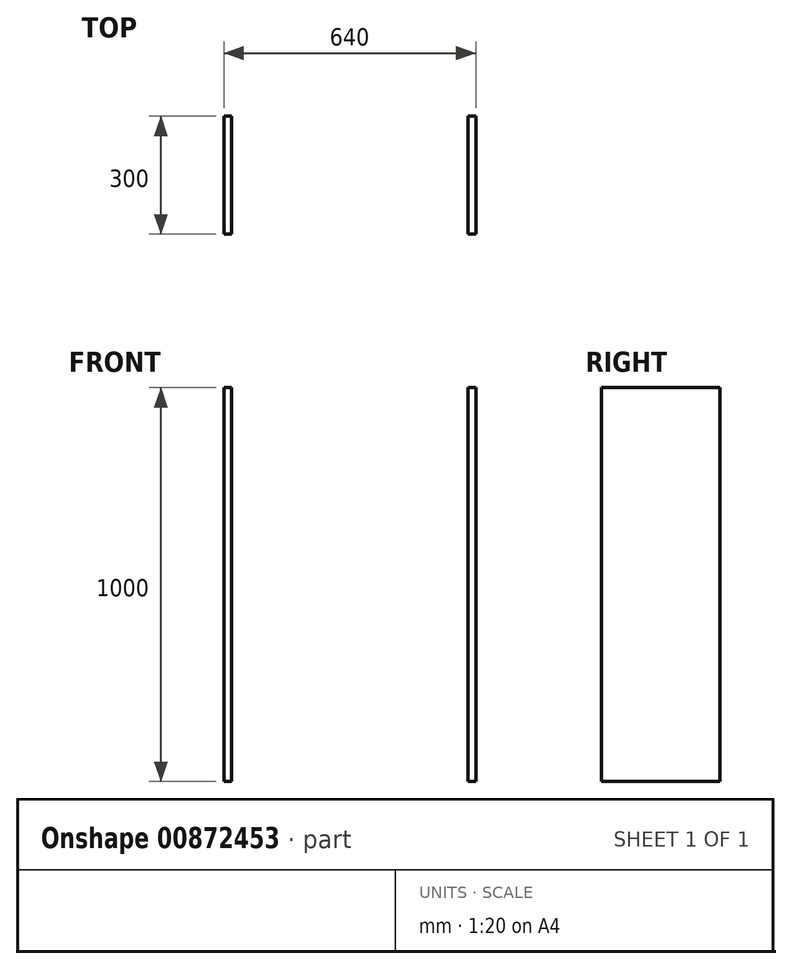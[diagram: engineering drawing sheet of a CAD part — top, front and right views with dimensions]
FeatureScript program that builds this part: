
annotation { "Feature Type Name" : "Feature", "Feature Type Description" : "" }
export const myFeature = defineFeature(function(context is Context, id is Id, definition is map)
    precondition{}
    {
        {
            var Q0;
            Q0=qCreatedBy(makeId("Right.planeOp"),FACE);
            cPlane(context, id + "F0", {"entities" : qUnion([Q0]), "cplaneType" : CPlaneType.OFFSET, "offset" : 300 * mm, "oppositeDirection" : true, "width" : 150 * mm, "height" : 150 * mm});
        }
        {
            var Q0;
            Q0=qCreatedBy(makeId("Right.planeOp"),FACE);
            cPlane(context, id + "F1", {"entities" : qUnion([Q0]), "cplaneType" : CPlaneType.OFFSET, "offset" : 300 * mm, "width" : 150 * mm, "height" : 150 * mm});
        }
        {
            var Q0;
            Q0=qCreatedBy(id+"F0.planeOp",FACE);
            var sketch = newSketch(context, id + "F2", { "sketchPlane" : qUnion([Q0])});
            skLineSegment(sketch, "E0", {"start": v(-400, 500) * mm, "end": v(-100, 500) * mm});
            skLineSegment(sketch, "E1", {"start": v(-100, 500) * mm, "end": v(-100, -500) * mm});
            skLineSegment(sketch, "E2", {"start": v(-100, -500) * mm, "end": v(-400, -500) * mm});
            skLineSegment(sketch, "E3", {"start": v(-400, -500) * mm, "end": v(-400, 500) * mm});
            skSolve(sketch);
        }
        {
            var Q0;
            Q0=qCreatedBy(id+"F1.planeOp",FACE);
            var sketch = newSketch(context, id + "F3", { "sketchPlane" : qUnion([Q0])});
            skLineSegment(sketch, "E4", {"start": v(-400, 500) * mm, "end": v(-100, 500) * mm});
            skLineSegment(sketch, "E5", {"start": v(-100, 500) * mm, "end": v(-100, -500) * mm});
            skLineSegment(sketch, "E6", {"start": v(-100, -500) * mm, "end": v(-400, -500) * mm});
            skLineSegment(sketch, "E7", {"start": v(-400, -500) * mm, "end": v(-400, 500) * mm});
            skSolve(sketch);
        }
        {
            var Q0;
            Q0=makeQuery(id+"F2.imprint","IMPRINT",FACE,{"disambiguationData":[TD([[makeQuery(id+"F2.imprint","IMPRINT",EDGE,{"derivedFrom":sQuery(id+"F2.wireOp",EDGE,"E0")}),-1.0]])]});
            extrude(context, id + "F4", {"entities" : qUnion([Q0]), "oppositeDirection" : true, "depth" : 20 * mm, "offsetDistance" : 25 * mm});
        }
        {
            var Q0;
            Q0=makeQuery(id+"F3.imprint","IMPRINT",FACE,{"disambiguationData":[TD([[makeQuery(id+"F3.imprint","IMPRINT",EDGE,{"derivedFrom":sQuery(id+"F3.wireOp",EDGE,"E4")}),-1.0]])]});
            extrude(context, id + "F5", {"entities" : qUnion([Q0]), "depth" : 20 * mm, "offsetDistance" : 25 * mm});
        }
    });
